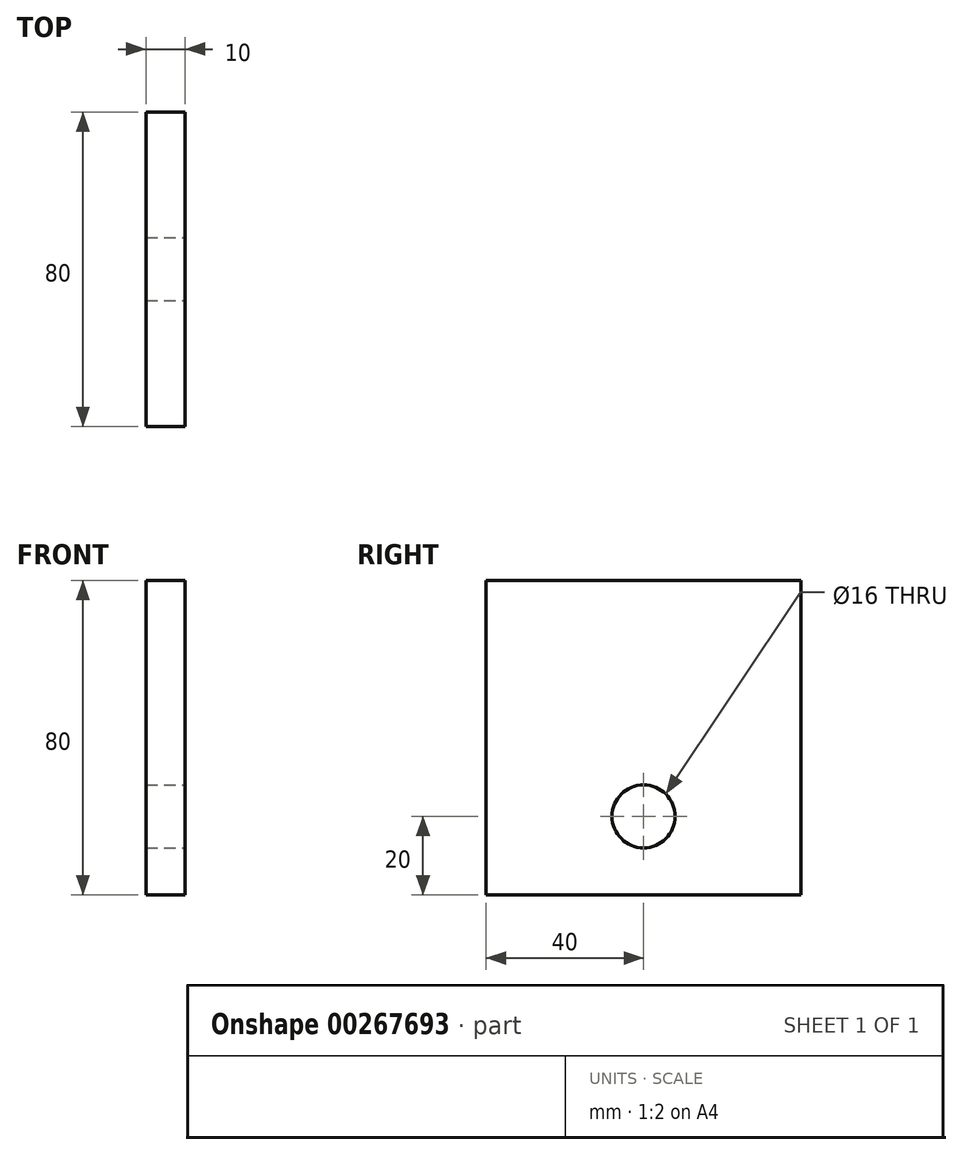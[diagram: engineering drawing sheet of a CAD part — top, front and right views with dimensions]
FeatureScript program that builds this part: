
annotation { "Feature Type Name" : "Feature", "Feature Type Description" : "" }
export const myFeature = defineFeature(function(context is Context, id is Id, definition is map)
    precondition{}
    {
        {
            var Q0;
            Q0=qCreatedBy(makeId("Front.planeOp"),FACE);
            var sketch = newSketch(context, id + "F0", { "sketchPlane" : qUnion([Q0])});
            skLineSegment(sketch, "E0.bottom", {"start": v(5, 40) * mm, "end": v(-5, 40) * mm});
            skLineSegment(sketch, "E0.top", {"start": v(5, -40) * mm, "end": v(-5, -40) * mm});
            skLineSegment(sketch, "E0.left", {"start": v(5, 40) * mm, "end": v(5, -40) * mm});
            skLineSegment(sketch, "E0.right", {"start": v(-5, 40) * mm, "end": v(-5, -40) * mm});
            skPoint(sketch, "E0.middle", {"position": v(0, 0) * mm});
            skSolve(sketch);
        }
        {
            var Q0;
            Q0 = qSketchRegion(id + "F0", true);
            extrude(context, id + "F1", {"entities" : qUnion([Q0]), "oppositeDirection" : true, "depth" : 80 * mm});
        }
        {
            var Q0;
            Q0=makeQuery(id+"F1.opExtrude","SWEPT_FACE",FACE,{"disambiguationData":[OSD([sQuery(id+"F0.wireOp",EDGE,"E0.left")])]});
            var sketch = newSketch(context, id + "F2", { "sketchPlane" : qUnion([Q0])});
            skCircle(sketch, "E1", {"center": v(40, -20) * mm, "radius": 8 * mm});
            skSolve(sketch);
        }
        {
            var Q0;
            Q0=makeQuery(id+"F2.imprint","IMPRINT",FACE,{"disambiguationData":[TD([[makeQuery(id+"F2.imprint","IMPRINT",EDGE,{"derivedFrom":sQuery(id+"F2.wireOp",EDGE,"E1")}),1.0]])]});
            extrude(context, id + "F3", {"entities" : qUnion([Q0]), "operationType" : NewBodyOperationType.REMOVE, "endBound" : BoundingType.THROUGH_ALL, "oppositeDirection" : true, "depth" : 25 * mm});
        }
    });
